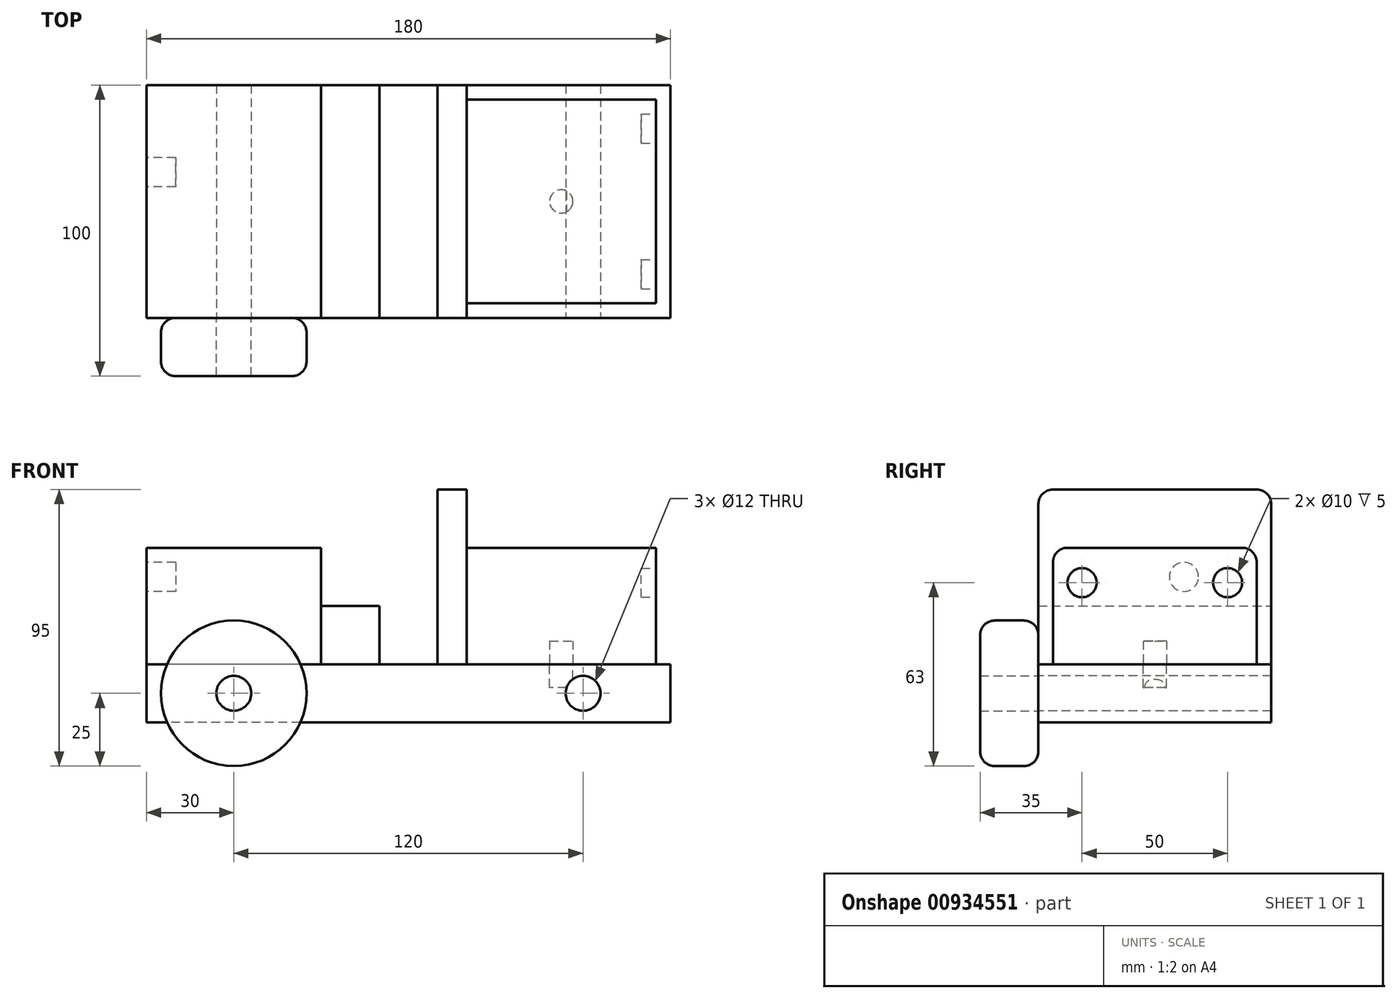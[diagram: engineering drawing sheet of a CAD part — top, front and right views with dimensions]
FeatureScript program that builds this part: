
annotation { "Feature Type Name" : "Feature", "Feature Type Description" : "" }
export const myFeature = defineFeature(function(context is Context, id is Id, definition is map)
    precondition{}
    {
        {
            var Q0;
            Q0=qCreatedBy(makeId("Top.planeOp"),FACE);
            var sketch = newSketch(context, id + "F0", { "sketchPlane" : qUnion([Q0])});
            skLineSegment(sketch, "E0.bottom", {"start": v(90, 40) * mm, "end": v(-90, 40) * mm});
            skLineSegment(sketch, "E0.top", {"start": v(90, -40) * mm, "end": v(-90, -40) * mm});
            skLineSegment(sketch, "E0.left", {"start": v(90, 40) * mm, "end": v(90, -40) * mm});
            skLineSegment(sketch, "E0.right", {"start": v(-90, 40) * mm, "end": v(-90, -40) * mm});
            skPoint(sketch, "E0.middle", {"position": v(0, 0) * mm});
            skSolve(sketch);
        }
        {
            var Q0;
            Q0 = qSketchRegion(id + "F0", true);
            extrude(context, id + "F1", {"entities" : qUnion([Q0]), "depth" : 20 * mm, "offsetDistance" : 25 * mm});
        }
        {
            var Q0;
            Q0=makeQuery(id+"F1.opExtrude","SWEPT_FACE",FACE,{"disambiguationData":[OSD([sQuery(id+"F0.wireOp",EDGE,"E0.top")])]});
            var sketch = newSketch(context, id + "F2", { "sketchPlane" : qUnion([Q0])});
            skCircle(sketch, "E1", {"center": v(-60, 10) * mm, "radius": 6 * mm});
            skPoint(sketch, "E1.centerSnap0", {"position": v(-90, 10) * mm});
            skCircle(sketch, "E2", {"center": v(60, 10) * mm, "radius": 6 * mm});
            skPoint(sketch, "E2.centerSnap0", {"position": v(90, 10) * mm});
            skSolve(sketch);
        }
        {
            var Q0;
            Q0 = qSketchRegion(id + "F2", true);
            extrude(context, id + "F3", {"entities" : qUnion([Q0]), "operationType" : NewBodyOperationType.REMOVE, "endBound" : BoundingType.THROUGH_ALL, "oppositeDirection" : true, "depth" : 25 * mm, "offsetDistance" : 25 * mm});
        }
        {
            var Q0;
            Q0=makeQuery(id+"F1.opExtrude","CAP_FACE",FACE,{"disambiguationData":[OSD([sQuery(id+"F0.wireOp",EDGE,"E0.bottom"),sQuery(id+"F0.wireOp",EDGE,"E0.top"),sQuery(id+"F0.wireOp",EDGE,"E0.left"),sQuery(id+"F0.wireOp",EDGE,"E0.right")])],"isStart":false});
            var sketch = newSketch(context, id + "F4", { "sketchPlane" : qUnion([Q0])});
            skLineSegment(sketch, "E3.bottom", {"start": v(-90, -40) * mm, "end": v(-30, -40) * mm});
            skLineSegment(sketch, "E3.top", {"start": v(-90, 40) * mm, "end": v(-30, 40) * mm});
            skLineSegment(sketch, "E3.left", {"start": v(-90, -40) * mm, "end": v(-90, 40) * mm});
            skLineSegment(sketch, "E3.right", {"start": v(-30, -40) * mm, "end": v(-30, 40) * mm});
            skSolve(sketch);
        }
        {
            var Q0;
            Q0 = qSketchRegion(id + "F4", true);
            extrude(context, id + "F5", {"entities" : qUnion([Q0]), "depth" : 40 * mm, "offsetDistance" : 25 * mm});
        }
        {
            var Q0;
            Q0=makeQuery(id+"F1.opExtrude","CAP_FACE",FACE,{"disambiguationData":[OSD([sQuery(id+"F0.wireOp",EDGE,"E0.bottom"),sQuery(id+"F0.wireOp",EDGE,"E0.top"),sQuery(id+"F0.wireOp",EDGE,"E0.left"),sQuery(id+"F0.wireOp",EDGE,"E0.right")])],"isStart":false});
            var sketch = newSketch(context, id + "F6", { "sketchPlane" : qUnion([Q0])});
            skLineSegment(sketch, "E4.bottom", {"start": v(-30, -40) * mm, "end": v(-10, -40) * mm});
            skLineSegment(sketch, "E4.top", {"start": v(-30, 40) * mm, "end": v(-10, 40) * mm});
            skLineSegment(sketch, "E4.left", {"start": v(-30, -40) * mm, "end": v(-30, 40) * mm});
            skLineSegment(sketch, "E4.right", {"start": v(-10, -40) * mm, "end": v(-10, 40) * mm});
            skSolve(sketch);
        }
        {
            var Q0;
            Q0 = qSketchRegion(id + "F6", true);
            extrude(context, id + "F7", {"entities" : qUnion([Q0]), "depth" : 20 * mm, "offsetDistance" : 25 * mm});
        }
        {
            var Q0;
            Q0=makeQuery(id+"F1.opExtrude","CAP_FACE",FACE,{"disambiguationData":[OSD([sQuery(id+"F0.wireOp",EDGE,"E0.bottom"),sQuery(id+"F0.wireOp",EDGE,"E0.top"),sQuery(id+"F0.wireOp",EDGE,"E0.left"),sQuery(id+"F0.wireOp",EDGE,"E0.right")])],"isStart":false});
            var sketch = newSketch(context, id + "F8", { "sketchPlane" : qUnion([Q0])});
            skLineSegment(sketch, "E5.bottom", {"start": v(85, -35) * mm, "end": v(20, -35) * mm});
            skLineSegment(sketch, "E5.top", {"start": v(85, 35) * mm, "end": v(20, 35) * mm});
            skLineSegment(sketch, "E5.left", {"start": v(85, -35) * mm, "end": v(85, 35) * mm});
            skLineSegment(sketch, "E5.right", {"start": v(20, -35) * mm, "end": v(20, 35) * mm});
            skSolve(sketch);
        }
        {
            var Q0;
            Q0 = qSketchRegion(id + "F8", true);
            extrude(context, id + "F9", {"entities" : qUnion([Q0]), "depth" : 40 * mm, "offsetDistance" : 25 * mm});
        }
        {
            var Q0;
            Q0=makeQuery(id+"F9.opExtrude","SWEPT_FACE",FACE,{"disambiguationData":[OSD([sQuery(id+"F8.wireOp",EDGE,"E5.left")])]});
            var sketch = newSketch(context, id + "F10", { "sketchPlane" : qUnion([Q0])});
            skCircle(sketch, "E6", {"center": v(-25, 48) * mm, "radius": 5 * mm});
            skCircle(sketch, "E7", {"center": v(25, 48) * mm, "radius": 5 * mm});
            skSolve(sketch);
        }
        {
            var Q0;
            Q0 = qSketchRegion(id + "F10", true);
            extrude(context, id + "F11", {"entities" : qUnion([Q0]), "operationType" : NewBodyOperationType.REMOVE, "oppositeDirection" : true, "depth" : 5 * mm, "offsetDistance" : 25 * mm});
        }
        {
            var Q0;
            Q0=makeQuery(id+"F1.opExtrude","CAP_FACE",FACE,{"disambiguationData":[OSD([sQuery(id+"F0.wireOp",EDGE,"E0.bottom"),sQuery(id+"F0.wireOp",EDGE,"E0.top"),sQuery(id+"F0.wireOp",EDGE,"E0.left"),sQuery(id+"F0.wireOp",EDGE,"E0.right")])],"isStart":false});
            var sketch = newSketch(context, id + "F12", { "sketchPlane" : qUnion([Q0])});
            skLineSegment(sketch, "E8.bottom", {"start": v(20, -40) * mm, "end": v(10, -40) * mm});
            skLineSegment(sketch, "E8.top", {"start": v(20, 40) * mm, "end": v(10, 40) * mm});
            skLineSegment(sketch, "E8.left", {"start": v(20, -40) * mm, "end": v(20, 40) * mm});
            skLineSegment(sketch, "E8.right", {"start": v(10, -40) * mm, "end": v(10, 40) * mm});
            skSolve(sketch);
        }
        {
            var Q0;
            Q0 = qSketchRegion(id + "F12", true);
            extrude(context, id + "F13", {"entities" : qUnion([Q0]), "depth" : 60 * mm, "offsetDistance" : 25 * mm});
        }
        {
            var Q0;
            Q0=makeQuery(id+"F1.opExtrude","SWEPT_FACE",FACE,{"disambiguationData":[OSD([sQuery(id+"F0.wireOp",EDGE,"E0.top")])]});
            var sketch = newSketch(context, id + "F14", { "sketchPlane" : qUnion([Q0])});
            skCircle(sketch, "E9.0", {"center": v(-60, 10) * mm, "radius": 6 * mm});
            skCircle(sketch, "E10", {"center": v(-60, 10) * mm, "radius": 25 * mm});
            skSolve(sketch);
        }
        {
            var Q0;
            Q0 = qSketchRegion(id + "F14", true);
            extrude(context, id + "F15", {"entities" : qUnion([Q0]), "depth" : 20 * mm, "offsetDistance" : 25 * mm});
        }
        {
            var Q0;
            Q0=makeQuery(id+"F15.opExtrude","SWEPT_FACE",FACE,{"disambiguationData":[OSD([sQuery(id+"F14.wireOp",EDGE,"E10")])]});
            fillet(context, id + "F16", {"entities" : qUnion([Q0]), "radius" : 5 * mm, "tangentPropagation" : true, "allowEdgeOverflow" : false});
        }
        {
            var Q0;
            Q0=makeQuery(id+"F5.opExtrude","SWEPT_FACE",FACE,{"disambiguationData":[OSD([sQuery(id+"F4.wireOp",EDGE,"E3.left")])]});
            var sketch = newSketch(context, id + "F17", { "sketchPlane" : qUnion([Q0])});
            skCircle(sketch, "E11", {"center": v(-10, 50) * mm, "radius": 5 * mm});
            skSolve(sketch);
        }
        {
            var Q0;
            Q0 = qSketchRegion(id + "F17", true);
            extrude(context, id + "F18", {"entities" : qUnion([Q0]), "operationType" : NewBodyOperationType.REMOVE, "oppositeDirection" : true, "depth" : 10 * mm, "offsetDistance" : 25 * mm});
        }
        {
            var Q0;
            Q0=makeQuery(id+"F9.opExtrude","CAP_EDGE",EDGE,{"disambiguationData":[OSD([sQuery(id+"F8.wireOp",EDGE,"E5.bottom")])],"isStart":false});
            var Q1;
            Q1=makeQuery(id+"F9.opExtrude","CAP_EDGE",EDGE,{"disambiguationData":[OSD([sQuery(id+"F8.wireOp",EDGE,"E5.top")])],"isStart":false});
            fillet(context, id + "F19", {"entities" : qUnion([Q0, Q1]), "radius" : 5 * mm, "tangentPropagation" : true, "allowEdgeOverflow" : false});
        }
        {
            var Q0;
            Q0=makeQuery(id+"F13.opExtrude","CAP_EDGE",EDGE,{"disambiguationData":[OSD([sQuery(id+"F12.wireOp",EDGE,"E8.bottom")])],"isStart":false});
            var Q1;
            Q1=makeQuery(id+"F13.opExtrude","CAP_EDGE",EDGE,{"disambiguationData":[OSD([sQuery(id+"F12.wireOp",EDGE,"E8.top")])],"isStart":false});
            fillet(context, id + "F20", {"entities" : qUnion([Q0, Q1]), "radius" : 5 * mm, "tangentPropagation" : true, "allowEdgeOverflow" : false});
        }
        {
            var Q0;
            Q0=makeQuery(id+"F9.opExtrude","CAP_FACE",FACE,{"disambiguationData":[OSD([sQuery(id+"F8.wireOp",EDGE,"E5.bottom"),sQuery(id+"F8.wireOp",EDGE,"E5.top"),sQuery(id+"F8.wireOp",EDGE,"E5.left"),sQuery(id+"F8.wireOp",EDGE,"E5.right")])],"isStart":true});
            var sketch = newSketch(context, id + "F21", { "sketchPlane" : qUnion([Q0])});
            skLineSegment(sketch, "E12", {"start": v(85, 35) * mm, "end": v(20, -35) * mm});
            skCircle(sketch, "E13", {"center": v(52.5, 0) * mm, "radius": 4 * mm});
            skSolve(sketch);
        }
        {
            var Q0;
            Q0 = qSketchRegion(id + "F21", true);
            extrude(context, id + "F22", {"entities" : qUnion([Q0]), "operationType" : NewBodyOperationType.REMOVE, "oppositeDirection" : true, "depth" : 8 * mm, "offsetDistance" : 25 * mm});
        }
        {
            var Q0;
            Q0=makeQuery(id+"F1.opExtrude","CAP_FACE",FACE,{"disambiguationData":[OSD([sQuery(id+"F0.wireOp",EDGE,"E0.bottom"),sQuery(id+"F0.wireOp",EDGE,"E0.top"),sQuery(id+"F0.wireOp",EDGE,"E0.left"),sQuery(id+"F0.wireOp",EDGE,"E0.right")])],"isStart":false});
            var sketch = newSketch(context, id + "F23", { "sketchPlane" : qUnion([Q0])});
            skCircle(sketch, "E14.0", {"center": v(52.5, 0) * mm, "radius": 4 * mm});
            skSolve(sketch);
        }
        {
            var Q0;
            Q0 = qSketchRegion(id + "F23", true);
            extrude(context, id + "F24", {"entities" : qUnion([Q0]), "operationType" : NewBodyOperationType.REMOVE, "oppositeDirection" : true, "depth" : 8 * mm, "offsetDistance" : 25 * mm});
        }
    });
